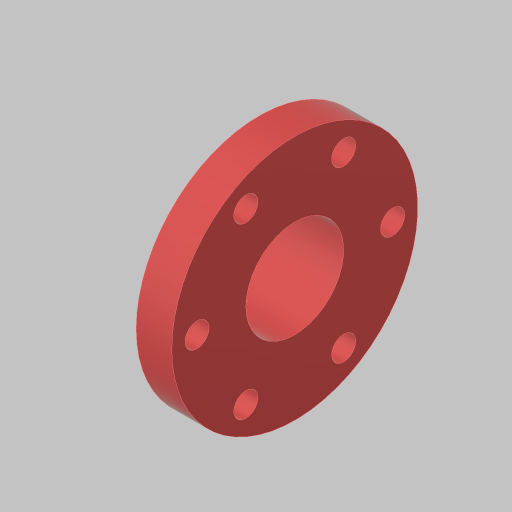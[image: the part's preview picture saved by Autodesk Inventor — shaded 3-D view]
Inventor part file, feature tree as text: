
AUTODESK INVENTOR PART (.ipt)
format: ipt  version: 2023.5 (Build 275446000, 446)  size: 243,200 bytes
history: native  units: in
note: dims shown in document units (in); Inventor stores cm internally (conversion verified against a paired STEP export)
features: sketch x4, extrude x3, hole x3, projected_geometry x1, other x1
ambient origin geometry x8: Origin, YZ Plane, XZ Plane, XY Plane, X Axis, Y Axis, Z Axis, Center Point
bodies: Solid1 (feature_tree)
feature tree (12):
  sketch  "Sketch1"  dims[d0=0.875in d1=2.0in d2=0.0in]
  extrude  "Extrusion1"  Depth=2.0in TaperAngle=0.0deg
  sketch  "Sketch2"  dims[d3=0.1562in]
  hole  "Hole1"  [1 undecoded]
  hole  "Hole2"  [1 undecoded]
  extrude  "Extrusion2"  Depth=1.0in TaperAngle=360.0deg
  hole  "Hole4"  [1 undecoded]
  extrude  "Extrusion3"  [1 undecoded]
  sketch  "Sketch4"  dims[d4=0.156in d5=0.38in d6=0.385in d7=0.25in d8=0.563in d9=1.0in d10=0.8108in]
  projected_geometry  "Projected Loop1"
  sketch  "Sketch6"  dims[d11=0.145in d12=0.38in d13=0.375in d14=0.25in d15=0.5635in d16=1.0in d17=0.8108in d19=0.3189in d20=0.0in d37=1.75in d38=2.3622in d40=360.0deg d42=0.2165in d43=0.75in d44=0.375in d45=0.25in d46=0.5635in d47=1.0in d48=0.8108in d49=0.0in d50=0.0in]
  other  "Cut-Extrude8"
note: 4 required parameter values undecoded (feature->parameter linkage not recoverable at this tier; creation-order binding heuristic only, values carry confidence <= 0.55)
